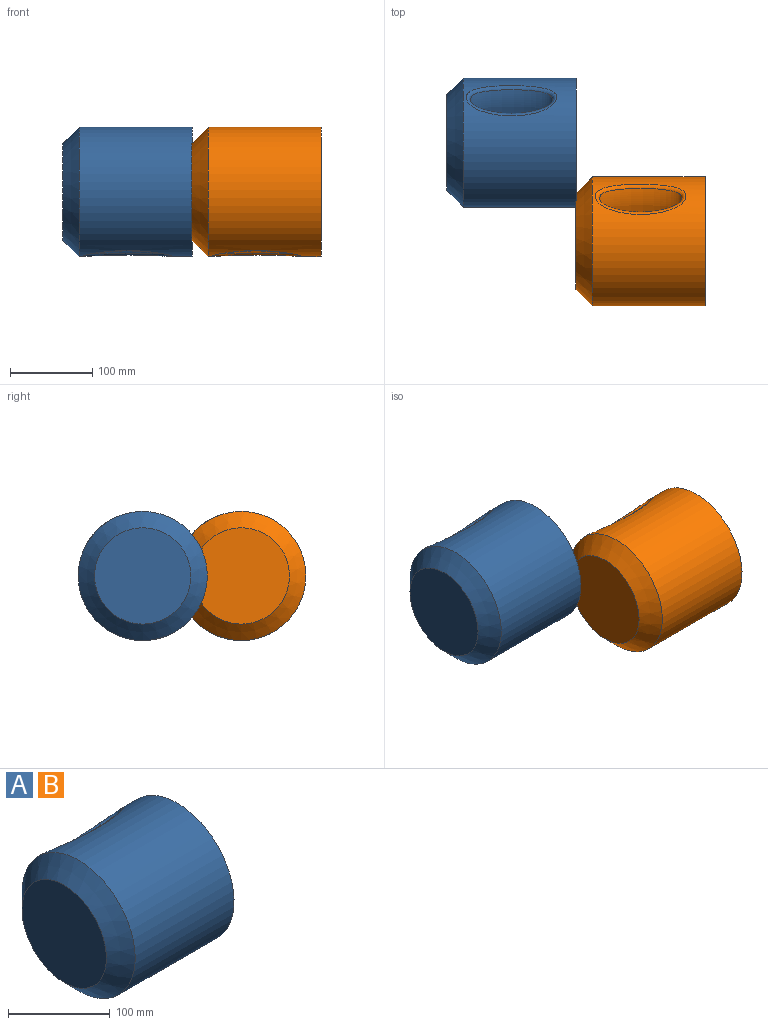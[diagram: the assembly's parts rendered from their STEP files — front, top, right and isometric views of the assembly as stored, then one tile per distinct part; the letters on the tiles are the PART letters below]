
ASSEMBLY  parts=2 mates=1
PART A: 21 faces, bbox 157.2x157.2x170.5 mm
  f0: plane 157.16x157.16mm, normal (1,0,0), area 8987.2mm2, adj f2,f8,f9,f10,f11,f12,f13,f14
  f1: plane 68.2x68.15mm, normal (1,0,0), area 3196.6mm2, adj f8,f9,f10,f11,f12,f13,f14,f15
  f2: cylinder r=78.58mm len=157.16mm, axis (-1,0,0), area 58668.9mm2, adj f0,f5,f6,f7
  f3: plane 117.16x117.16mm, normal (-1,0,0), area 10781.2mm2, adj f5
  f4: revolved ~161.37x100mm, area 33970.1mm2, adj f6,f7,f11,f18
  f5: cone r=78.58mm half-angle=45deg, axis (1,0,0), area 12187.9mm2, adj f2,f3
  f6: bspline ~110.17x50.27mm, area 2092.6mm2, adj f2,f4
  f7: bspline ~110.16x37.01mm, area 2092mm2, adj f2,f4
  f8: cone r=0mm half-angle=21.1deg, axis (1,0,0), area 1541.2mm2, adj f0,f1,f9,f20
  f9: cone r=0mm half-angle=21.1deg, axis (1,0,0), area 1541.2mm2, adj f0,f1,f8,f10
  f10: cone r=0mm half-angle=21.1deg, axis (1,0,0), area 1541.2mm2, adj f0,f1,f9,f11
  f11: cone r=0mm half-angle=21.1deg, axis (1,0,0), area 1461.5mm2, adj f0,f1,f4,f10,f12
  f12: cone r=0mm half-angle=21.1deg, axis (1,0,0), area 1541.1mm2, adj f0,f1,f11,f13
  f13: cone r=0mm half-angle=21.1deg, axis (1,0,0), area 1541.2mm2, adj f0,f1,f12,f14
  f14: cone r=0mm half-angle=21.1deg, axis (1,0,0), area 1541.2mm2, adj f0,f1,f13,f15
  f15: cone r=0mm half-angle=21.1deg, axis (1,0,0), area 1541.2mm2, adj f0,f1,f14,f16
  f16: cone r=0mm half-angle=21.1deg, axis (1,0,0), area 1541.2mm2, adj f0,f1,f15,f17
  f17: cone r=0mm half-angle=21.1deg, axis (1,0,0), area 1541.2mm2, adj f0,f1,f16,f18
  f18: cone r=0mm half-angle=21.1deg, axis (1,0,0), area 1461.5mm2, adj f0,f1,f4,f17,f19
  f19: cone r=0mm half-angle=21.1deg, axis (1,0,0), area 1541.1mm2, adj f0,f1,f18,f20
  f20: cone r=0mm half-angle=21.1deg, axis (1,0,0), area 1541.2mm2, adj f0,f1,f8,f19
PART B: same geometry as A
PLACE A t=(-165.94,116.76,-1.54)mm
PLACE B t=(-8.78,-3.24,-1.54)mm
MATE fastened A.f2 <-> B.f3  axis (-1,0,0) through (-8.78,241.37,-11.76)mm
